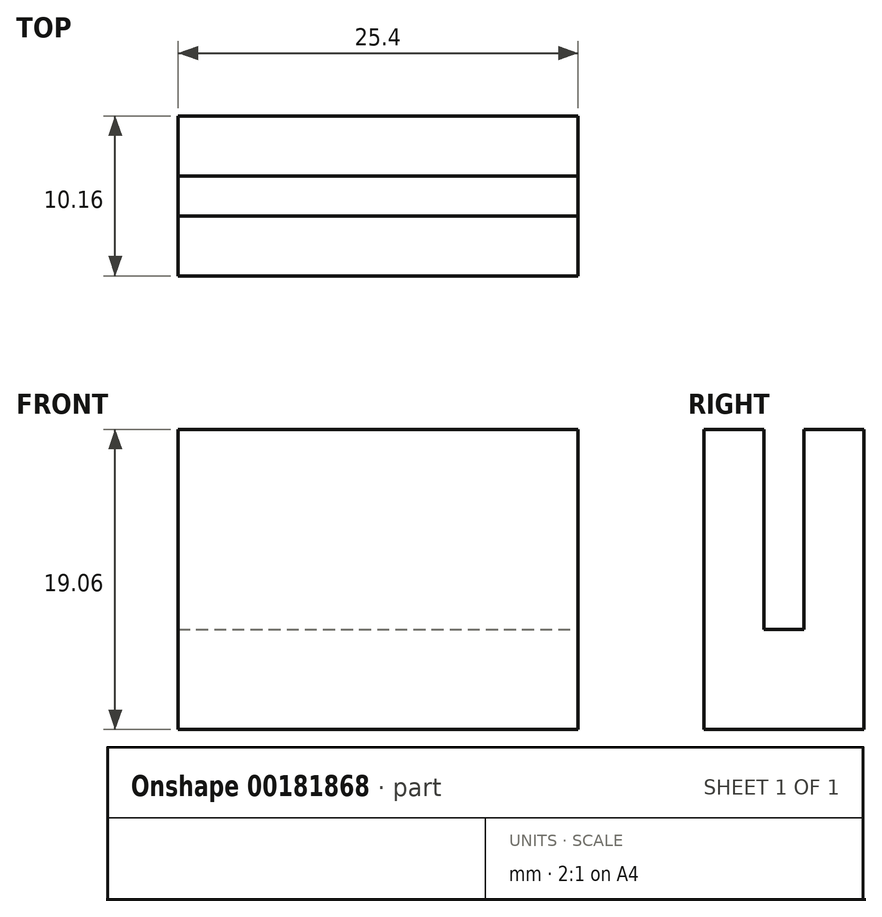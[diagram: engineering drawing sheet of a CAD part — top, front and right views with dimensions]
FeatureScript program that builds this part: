
annotation { "Feature Type Name" : "Feature", "Feature Type Description" : "" }
export const myFeature = defineFeature(function(context is Context, id is Id, definition is map)
    precondition{}
    {
        {
            var Q0;
            Q0=qCreatedBy(makeId("Front.planeOp"),FACE);
            var sketch = newSketch(context, id + "F0", { "sketchPlane" : qUnion([Q0])});
            skLineSegment(sketch, "E0.bottom", {"start": v(12.7, 9.53) * mm, "end": v(-12.7, 9.53) * mm});
            skLineSegment(sketch, "E0.top", {"start": v(12.7, -9.52) * mm, "end": v(-12.7, -9.52) * mm});
            skLineSegment(sketch, "E0.left", {"start": v(12.7, 9.53) * mm, "end": v(12.7, -9.52) * mm});
            skLineSegment(sketch, "E0.right", {"start": v(-12.7, 9.53) * mm, "end": v(-12.7, -9.52) * mm});
            skPoint(sketch, "E0.middle", {"position": v(0, 0) * mm});
            skSolve(sketch);
        }
        {
            var Q0;
            Q0=makeQuery(id+"F0.imprint","IMPRINT",FACE,{"disambiguationData":[TD([[makeQuery(id+"F0.imprint","IMPRINT",EDGE,{"derivedFrom":sQuery(id+"F0.wireOp",EDGE,"E0.bottom")}),1.0]])]});
            extrude(context, id + "F1", {"entities" : qUnion([Q0]), "endBound" : BoundingType.SYMMETRIC, "depth" : 10.16 * mm});
        }
        {
            var Q0;
            Q0=makeQuery(id+"F1.opExtrude","SWEPT_FACE",FACE,{"disambiguationData":[OSD([sQuery(id+"F0.wireOp",EDGE,"E0.bottom")])]});
            var sketch = newSketch(context, id + "F2", { "sketchPlane" : qUnion([Q0])});
            skLineSegment(sketch, "E1.bottom", {"start": v(-12.7, 1.27) * mm, "end": v(12.7, 1.27) * mm});
            skLineSegment(sketch, "E1.top", {"start": v(-12.7, -1.27) * mm, "end": v(12.7, -1.27) * mm});
            skLineSegment(sketch, "E1.left", {"start": v(-12.7, 1.27) * mm, "end": v(-12.7, -1.27) * mm});
            skLineSegment(sketch, "E1.right", {"start": v(12.7, 1.27) * mm, "end": v(12.7, -1.27) * mm});
            skPoint(sketch, "E1.middle", {"position": v(0, 0) * mm});
            skSolve(sketch);
        }
        {
            var Q0;
            Q0=makeQuery(id+"F2.imprint","IMPRINT",FACE,{"disambiguationData":[TD([[makeQuery(id+"F2.imprint","IMPRINT",EDGE,{"derivedFrom":sQuery(id+"F2.wireOp",EDGE,"E1.bottom")}),-1.0]])]});
            extrude(context, id + "F3", {"entities" : qUnion([Q0]), "operationType" : NewBodyOperationType.REMOVE, "oppositeDirection" : true, "depth" : 12.7 * mm});
        }
    });
